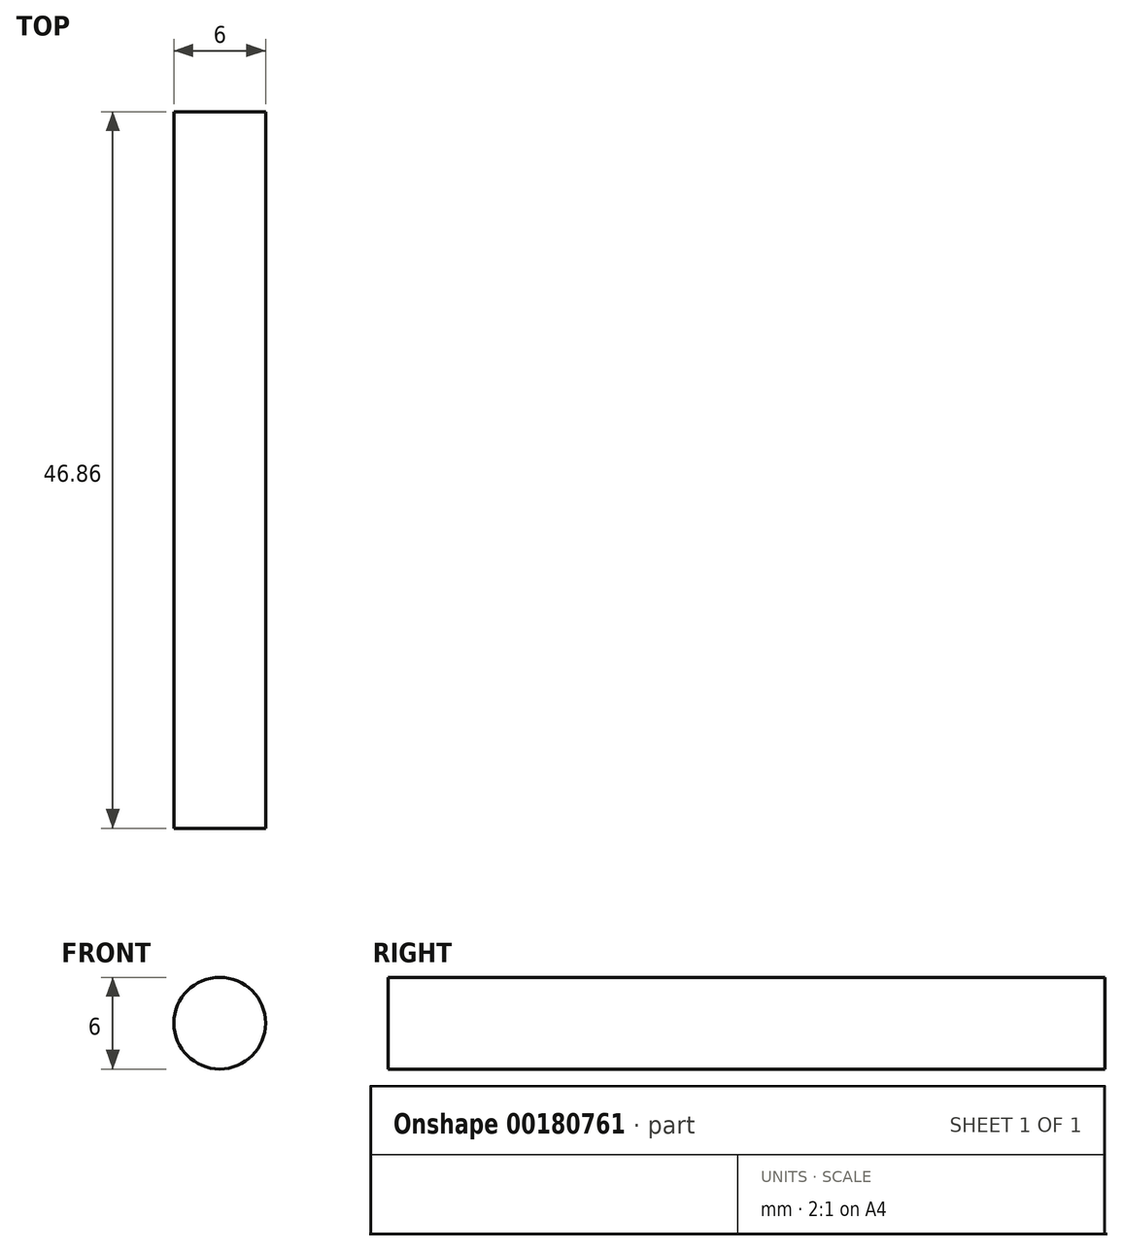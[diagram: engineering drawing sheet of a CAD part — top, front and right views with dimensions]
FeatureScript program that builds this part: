
annotation { "Feature Type Name" : "Feature", "Feature Type Description" : "" }
export const myFeature = defineFeature(function(context is Context, id is Id, definition is map)
    precondition{}
    {
        {
            var Q0;
            Q0=qCreatedBy(makeId("Front.planeOp"),FACE);
            var sketch = newSketch(context, id + "F0", { "sketchPlane" : qUnion([Q0])});
            skCircle(sketch, "E0", {"center": v(0, 0) * mm, "radius": 3 * mm});
            skSolve(sketch);
        }
        {
            var Q0;
            Q0 = qSketchRegion(id + "F0", true);
            extrude(context, id + "F1", {"entities" : qUnion([Q0]), "depth" : 46.86 * mm});
        }
    });
